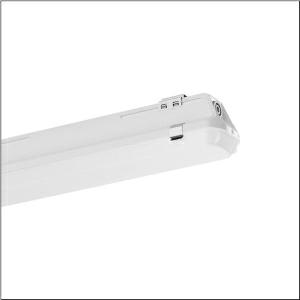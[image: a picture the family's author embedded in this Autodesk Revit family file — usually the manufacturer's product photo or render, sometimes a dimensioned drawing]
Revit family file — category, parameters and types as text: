
# Revit family: monsun_r__21_51fb10dp440b_4f1d
name_source: partatom
category: Lighting Fixtures
units: mm (PartAtom-declared; Revit-internal decimal feet)

## family parameters
Cut with Voids When Loaded = No
Host = Face
Light Source = No
Part Type = Normal
Room Calculation Point = No
Round Connector Dimension = Use Diameter
Shared = No

## types (1)
- --- (1 x LED, 4360 lm, 27.9 W, 4000K)
    Apparent Load = 28 VA
    CIE Flux Codes = 47 77 93 94 100
    Color Rendering = 80
    Color Temperature = 4000K
    Default Elevation = 1800 mm
    Description = Monsun® 21, damp-proof luminaire, chain hanger, primary optical cover: enclosure, of PMMA, light emission: direct distribution, primary light characteristic: symmetric, installation type: suspended mounting, surface-mounted, horizontal mounting, vertical mounting, LED, rated luminous flux: 4.360lm, luminous efficacy: 156lm/W, light colour: 840, colour temperature: 4000K, control gear: ECG DALI, with terminal, 5-pole, max. 2.5mm², mains connection: 220..240V, AC, 50/60Hz, rated input power: 28W, housing, of glass-fibre reinforced polyester, uncoated, bright grey, incl. chain hanger, length: 1.590mm, width: 90mm, height: 88mm, clip for enclosure, of stainless steel (V2A), ceiling mounting element, of stainless steel (V2A), chain hanger, of stainless steel (V2A), protection rating (complete): IP66, insulation class (complete): insulation class I (protective earthing), certification: CE, ENEC, VDE, UKCA, protection symbol: D, impact resistance: IK04, permissible operating ambient temperature: -25..+35°C, standard: EN 50419, EN 60598-2-1, corresponds to IFS (International Featured Standards) requirements for safety and quality in the food industry, for indoor or canopied outdoor use, no direct snow, no direct sun, no direct rain, contact your sales advisor before using the luminaires in applications with unclear chemical exposure, large temperature fluctuations or condensation-forming humidity, LABS conformity tested according to VDMA 24364:2018-05, packaging unit: 1 piece
    Height = 89 mm
    Lamp = 1 x LED
    Lamp Light Flux = 4360 lm
    Lamp Power = 27.9 W
    Lamp count = 1
    Length = 1590 mm
    Luminous efficacy = 156 lm/W
    Manufacturer = Siteco
    ModVariant = No
    Model = 51FB10DP440B
    Mounting Place = Ceiling
    Mounting Type = Surface mounted
    Number of Poles = 1
    OnlyDefault = Yes
    Power Factor = 1
    Product Name = Monsun® 21
    Product group = damp-proof luminaire
    ProductGroupID = 300
    Protection Class = Protection class I
    Protection Degree = IP 66
    RLX_Detail_Level = 1
    RLX_Emergency_Light_Flux = 0 lm
    RLX_Emergency_Type = 0
    RLX_Emergency_Type_DB = No
    RlxData = <blob elided: 92425 chars, md5=3b21fa53>
    Socket = socket
    Standby Power = 0 W
    System Light Flux = 4360 lm
    System Power = 28 W
    Type Comments = factory setting: luminous flux: 100 % | dim-lin: 254 | 184 mA
    Type Image = l_1319656.jpg
    URL = http://relux.com
    VarID = @adj_171393
    Voltage = 0 V
    Weight = 0.00 kg
    Width = 90 mm

## geometry (parser evidence)
native form markers: Blend x4, Sweep x12
no freeform markers — native parametric forms only
